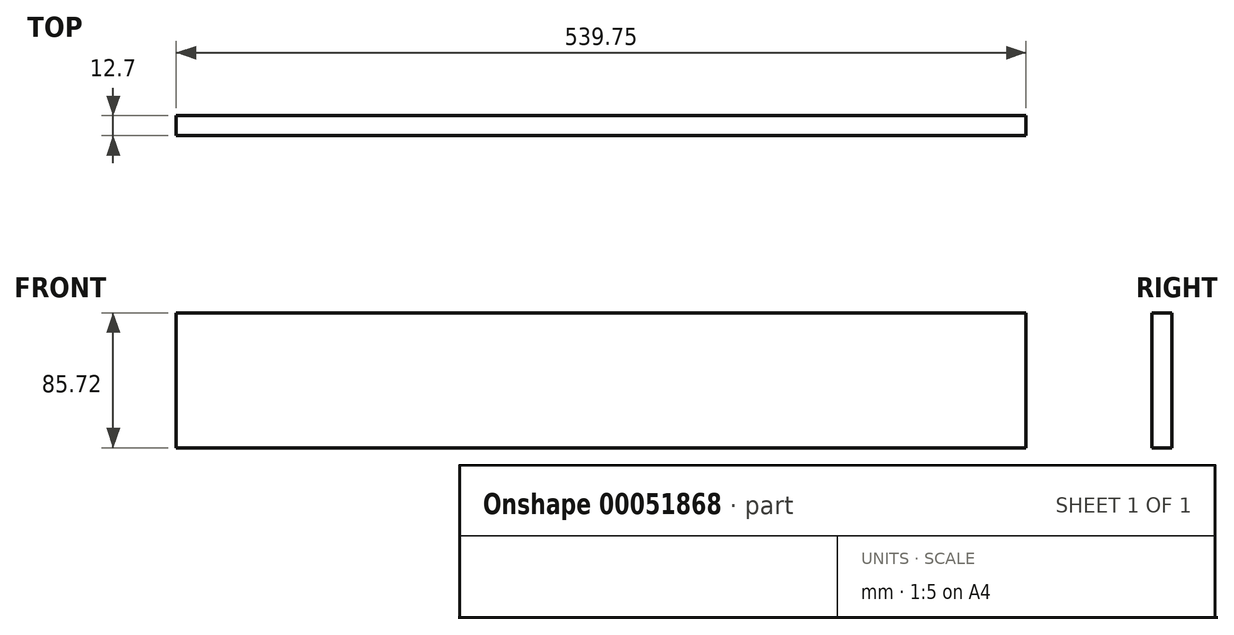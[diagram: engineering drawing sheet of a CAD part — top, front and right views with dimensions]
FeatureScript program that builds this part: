
annotation { "Feature Type Name" : "Feature", "Feature Type Description" : "" }
export const myFeature = defineFeature(function(context is Context, id is Id, definition is map)
    precondition{}
    {
        {
            var Q0;
            Q0=qCreatedBy(makeId("Front.planeOp"),FACE);
            var sketch = newSketch(context, id + "F0", { "sketchPlane" : qUnion([Q0])});
            skLineSegment(sketch, "E0.bottom", {"start": v(-254, 38.1) * mm, "end": v(285.75, 38.1) * mm});
            skLineSegment(sketch, "E0.top", {"start": v(-254, -47.62) * mm, "end": v(285.75, -47.62) * mm});
            skLineSegment(sketch, "E0.left", {"start": v(-254, 38.1) * mm, "end": v(-254, -47.62) * mm});
            skLineSegment(sketch, "E0.right", {"start": v(285.75, 38.1) * mm, "end": v(285.75, -47.62) * mm});
            skSolve(sketch);
        }
        {
            var Q0;
            Q0=makeQuery(id+"F0.imprint","IMPRINT",FACE,{"disambiguationData":[TD([[makeQuery(id+"F0.imprint","IMPRINT",EDGE,{"derivedFrom":sQuery(id+"F0.wireOp",EDGE,"E0.bottom")}),-1.0]])]});
            extrude(context, id + "F1", {"entities" : qUnion([Q0]), "depth" : 12.7 * mm});
        }
    });
